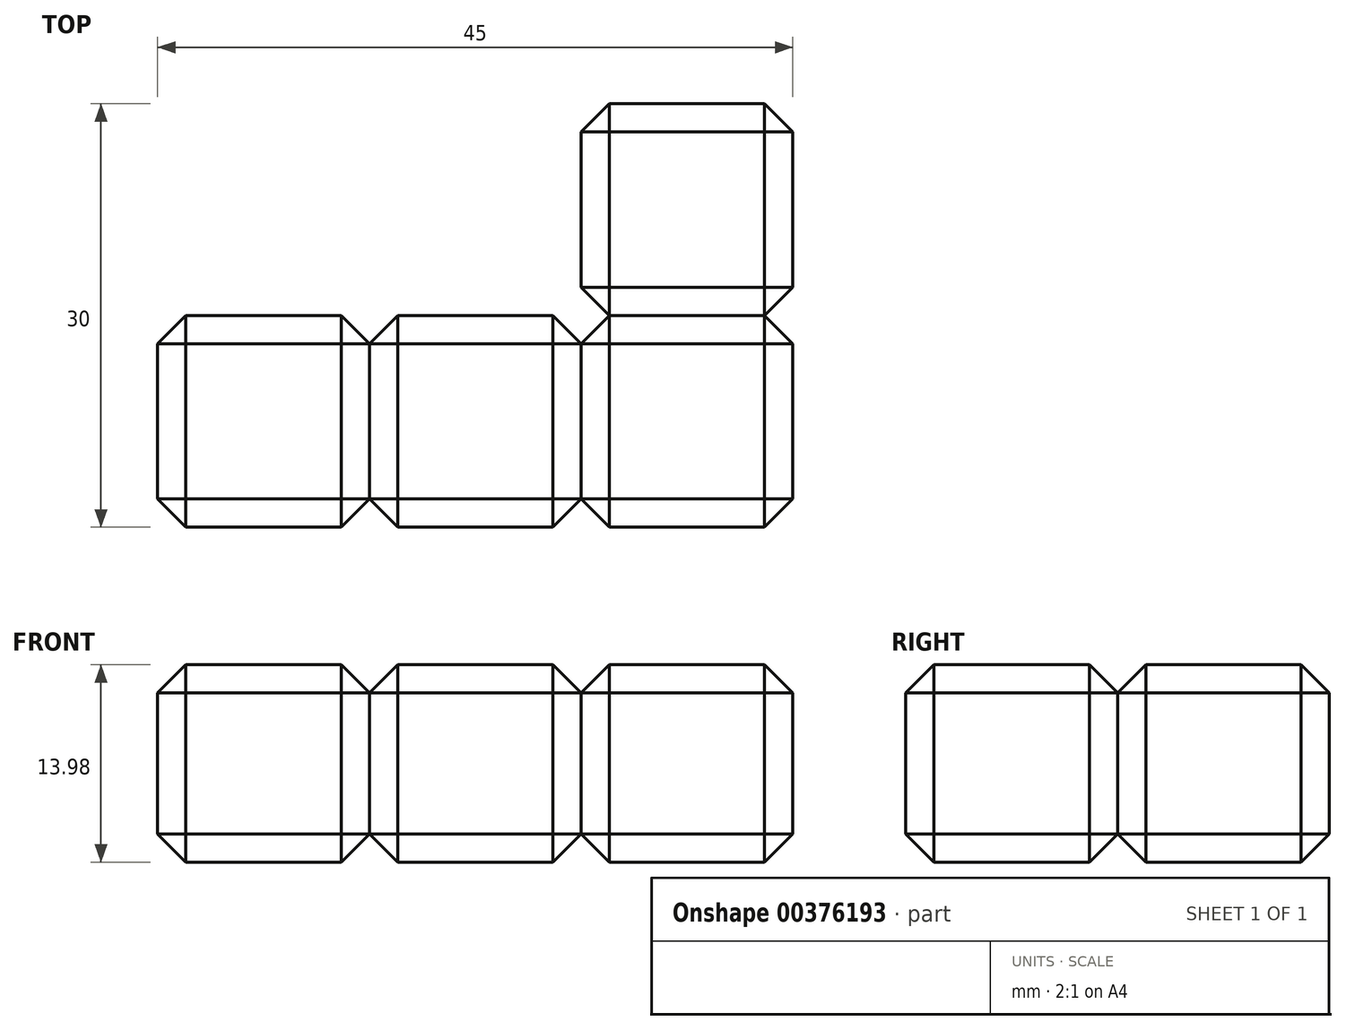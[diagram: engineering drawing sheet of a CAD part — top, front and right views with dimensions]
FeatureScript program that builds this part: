
annotation { "Feature Type Name" : "Feature", "Feature Type Description" : "" }
export const myFeature = defineFeature(function(context is Context, id is Id, definition is map)
    precondition{}
    {
        {
            var Q0;
            Q0=qCreatedBy(makeId("Front.planeOp"),FACE);
            var sketch = newSketch(context, id + "F0", { "sketchPlane" : qUnion([Q0])});
            skLineSegment(sketch, "E0.bottom", {"start": v(7.5, 6.99) * mm, "end": v(-7.5, 6.99) * mm});
            skLineSegment(sketch, "E0.top", {"start": v(7.5, -6.99) * mm, "end": v(-7.5, -6.99) * mm});
            skLineSegment(sketch, "E0.left", {"start": v(7.5, 6.99) * mm, "end": v(7.5, -6.99) * mm});
            skLineSegment(sketch, "E0.right", {"start": v(-7.5, 6.99) * mm, "end": v(-7.5, -6.99) * mm});
            skPoint(sketch, "E0.middle", {"position": v(0, 0) * mm});
            skSolve(sketch);
        }
        {
            var Q0;
            Q0 = qSketchRegion(id + "F0", true);
            extrude(context, id + "F1", {"entities" : qUnion([Q0]), "depth" : 15 * mm});
        }
        {
            var Q0;
            Q0=makeQuery(id+"F1.opExtrude","SWEPT_FACE",FACE,{"disambiguationData":[OSD([sQuery(id+"F0.wireOp",EDGE,"E0.right")])]});
            var Q1;
            Q1=makeQuery(id+"F1.opExtrude","CAP_FACE",FACE,{"disambiguationData":[OSD([sQuery(id+"F0.wireOp",EDGE,"E0.bottom"),sQuery(id+"F0.wireOp",EDGE,"E0.top"),sQuery(id+"F0.wireOp",EDGE,"E0.left"),sQuery(id+"F0.wireOp",EDGE,"E0.right")])],"isStart":false});
            var Q2;
            Q2=makeQuery(id+"F1.opExtrude","SWEPT_FACE",FACE,{"disambiguationData":[OSD([sQuery(id+"F0.wireOp",EDGE,"E0.bottom")])]});
            var Q3;
            Q3=makeQuery(id+"F1.opExtrude","CAP_FACE",FACE,{"disambiguationData":[OSD([sQuery(id+"F0.wireOp",EDGE,"E0.bottom"),sQuery(id+"F0.wireOp",EDGE,"E0.top"),sQuery(id+"F0.wireOp",EDGE,"E0.left"),sQuery(id+"F0.wireOp",EDGE,"E0.right")])],"isStart":true});
            var Q4;
            Q4=makeQuery(id+"F1.opExtrude","SWEPT_FACE",FACE,{"disambiguationData":[OSD([sQuery(id+"F0.wireOp",EDGE,"E0.top")])]});
            chamfer(context, id + "F2", {"entities" : qUnion([Q0, Q1, Q2, Q3, Q4]), "width" : 2 * mm, "tangentPropagation" : true});
        }
        {
            var Q0;
            Q0=makeQuery(id+"F1.opExtrude","SWEPT_BODY",BODY,{"disambiguationData":[OSD([sQuery(id+"F0.wireOp",EDGE,"E0.bottom"),sQuery(id+"F0.wireOp",EDGE,"E0.top"),sQuery(id+"F0.wireOp",EDGE,"E0.left"),sQuery(id+"F0.wireOp",EDGE,"E0.right")])]});
            transform(context, id + "F3", {"entities" : qUnion([Q0]), "transformType" : TransformType.TRANSLATION_3D, "dx" : 15 * mm, "dy" : 0 * mm, "dz" : 0 * mm, "makeCopy" : true});
        }
        {
            var Q0;
            Q0=makeQuery(id+"F3.opPattern","COPY",BODY,{"derivedFrom":makeQuery(id+"F1.opExtrude","SWEPT_BODY",BODY,{"disambiguationData":[OSD([sQuery(id+"F0.wireOp",EDGE,"E0.bottom"),sQuery(id+"F0.wireOp",EDGE,"E0.top"),sQuery(id+"F0.wireOp",EDGE,"E0.left"),sQuery(id+"F0.wireOp",EDGE,"E0.right")])]}),"instanceName":"1"});
            transform(context, id + "F4", {"entities" : qUnion([Q0]), "transformType" : TransformType.TRANSLATION_3D, "dx" : 15 * mm, "dy" : 0 * mm, "dz" : 0 * mm, "makeCopy" : true});
        }
        {
            var Q0;
            Q0=makeQuery(id+"F4.opPattern","COPY",BODY,{"derivedFrom":makeQuery(id+"F3.opPattern","COPY",BODY,{"derivedFrom":makeQuery(id+"F1.opExtrude","SWEPT_BODY",BODY,{"disambiguationData":[OSD([sQuery(id+"F0.wireOp",EDGE,"E0.bottom"),sQuery(id+"F0.wireOp",EDGE,"E0.top"),sQuery(id+"F0.wireOp",EDGE,"E0.left"),sQuery(id+"F0.wireOp",EDGE,"E0.right")])]}),"instanceName":"1"}),"instanceName":"1"});
            transform(context, id + "F5", {"entities" : qUnion([Q0]), "transformType" : TransformType.TRANSLATION_3D, "dx" : 0 * mm, "dy" : 15 * mm, "dz" : 0 * mm, "makeCopy" : true});
        }
    });
